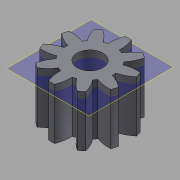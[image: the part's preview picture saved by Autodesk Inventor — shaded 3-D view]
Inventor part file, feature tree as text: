
AUTODESK INVENTOR PART (.ipt)
format: ipt  version: 2015 (Build 190159000, 159)  size: 162,816 bytes
history: native  units: in
note: dims shown in document units (in); Inventor stores cm internally (conversion verified against a paired STEP export)
features: other x13, sketch x3, plane x2
ambient origin geometry x8: Origin, YZ Plane, XZ Plane, XY Plane, X Axis, Y Axis, Z Axis, Center Point
bodies: Solid1 (feature_tree)
feature tree (18):
  other  "Spur Gear1"
  other  "Solid1::Spur Gear1"
  other  "TaggingFeature1"
  sketch  "Sketch1"  dims[d0=0.3937in]
  sketch  "Sketch2"  dims[d16=0.4528in d17=0.0in d41=0.0in d43=0.4528in d46=0.4528in d47=0.0in d48=0.0in]
  sketch  "Sketch3"
  plane  "XZ Plane_1"
  plane  "Work Plane2"
  other  "Z Axis_1"
  other  "Srf1"
  other  "Srf1::Derived"
  other  "Distance iMate"
  other  "Align iMate"
  other  "Mesh iMate"
  other  "Axis iMate"
  other  "Position iMate"
  other  "Mesh iMate2"
  other  "Start plane iMate"
